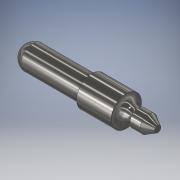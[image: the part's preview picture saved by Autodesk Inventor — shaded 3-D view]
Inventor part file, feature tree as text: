
AUTODESK INVENTOR PART (.ipt)
format: ipt  version: 2018.3 (Build 223284000, 284)  size: 148,992 bytes
history: native  units: in
note: dims shown in document units (in); Inventor stores cm internally (conversion verified against a paired STEP export)
features: sketch x2, revolve x1
ambient origin geometry x8: Origin, YZ Plane, XZ Plane, XY Plane, X Axis, Y Axis, Z Axis, Center Point
bodies: Body1 (feature_tree)
feature tree (3):
  sketch  "Sketch1"  dims[d0=0.025in d1=0.0645in]
  sketch  "Sketch2"  dims[d3=0.47in d4=0.115in d6=0.13in d8=0.222in d11=0.03in d13=0.025in d14=0.0645in d15=0.115in d19=90.0deg]
  revolve  "Revolution1"  [1 undecoded]
note: 1 required parameter value undecoded (feature->parameter linkage not recoverable at this tier; creation-order binding heuristic only, values carry confidence <= 0.55)
